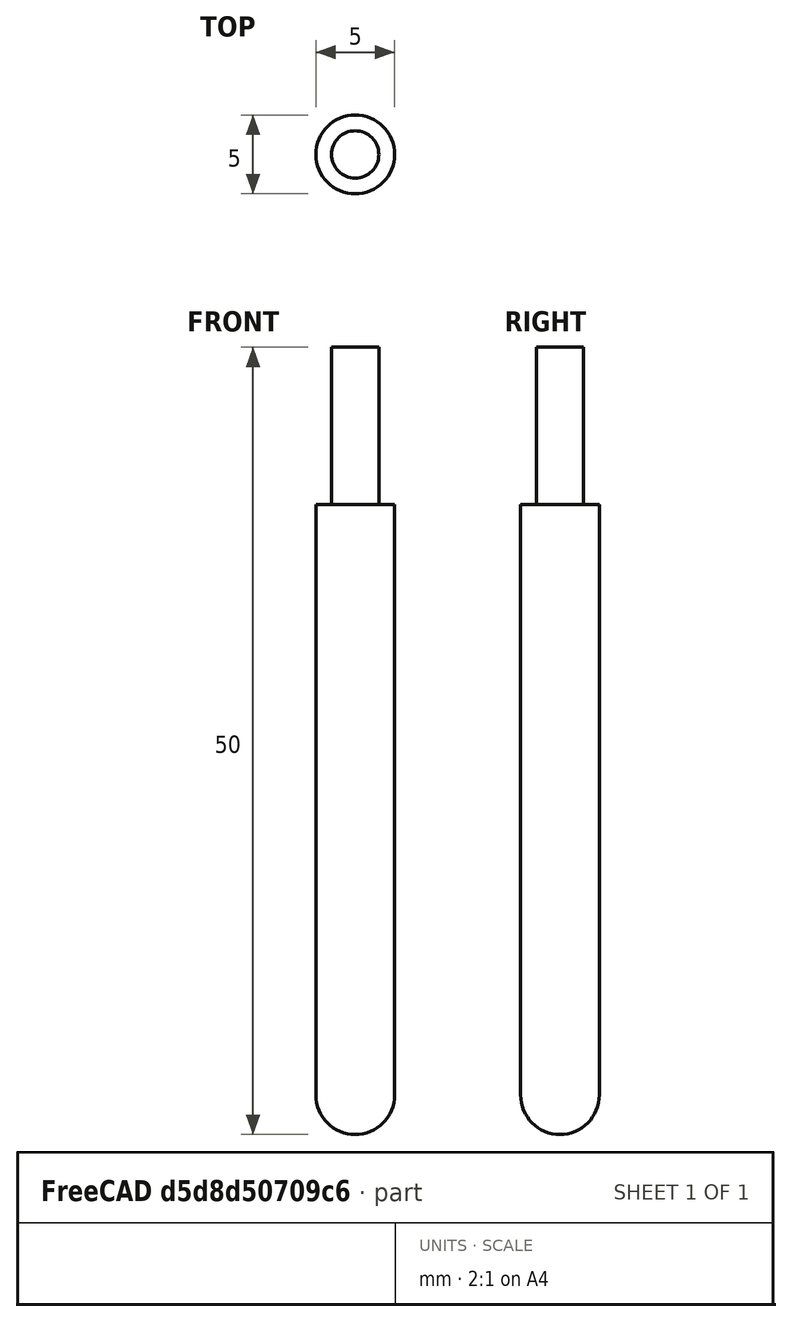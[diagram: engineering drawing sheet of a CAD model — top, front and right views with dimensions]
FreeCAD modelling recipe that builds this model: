
FCSTD DOCUMENT  (FreeCAD 0.19R24049 (Git))
Label: ballend
License: All rights reserved
LicenseURL: http://en.wikipedia.org/wiki/All_rights_reserved
objects: Sketcher::SketchObject×1, PartDesign::Revolution×1, App::FeaturePython×1, PartDesign::Body×1
note: 4 computed .brp shape members not serialized (recipe doc carries the construction recipe); baked Part::Feature solids carry a one-line shape summary decoded from their .brp

FEATURE [Sketcher::SketchObject] Sketch
  FullyConstrained = true
  MapMode = 5
  Placement = pos=(0,0,0) rot=(1,0,0;1.5708rad)
  Support = -> [XZ_Plane]
  expr: Constraints[10] = <<Attributes>>.ShankDiameter
  expr: Constraints[4] = <<Attributes>>.Length
  expr: Constraints[3] = <<Attributes>>.Diameter
  expr: Constraints[17] = <<Attributes>>.CuttingEdgeHeight
  sketch-geometry (8):
    g0: LineSegment StartX=-9e-16 StartY=50 StartZ=0 EndX=-9e-16 EndY=0 EndZ=0
    g1: LineSegment StartX=2.5 StartY=2.5 StartZ=0 EndX=2.5 EndY=40 EndZ=0
    g2: LineSegment StartX=1.5 StartY=50 StartZ=0 EndX=-9e-16 EndY=50 EndZ=0
    g3: LineSegment StartX=2.5 StartY=0 StartZ=0 EndX=-2.5 EndY=0 EndZ=0
    g4: LineSegment StartX=1.5 StartY=40.01 StartZ=0 EndX=2.5 EndY=40 EndZ=0
    g5: LineSegment StartX=1.5 StartY=50 StartZ=0 EndX=1.5 EndY=40.01 EndZ=0
    g6: LineSegment StartX=-1.5 StartY=50 StartZ=0 EndX=1.5 EndY=50 EndZ=0
    g7: ArcOfCircle CenterX=-5e-16 CenterY=2.5 CenterZ=0 NormalX=0 NormalY=0 NormalZ=1 AngleXU=0 Radius=2.5 StartAngle=4.71239 EndAngle=6.28319
  constraints (21):
    c: Vertical(g0)
    c: Vertical(g1)
    c: Horizontal(g2)
    c: DistanceX(g3,g3) = 5
    c: DistanceY(g3,g2) = 50
    c: Coincident(g1,g4)
    c: Vertical(g5)
    c: Coincident(g2,g5)
    c: Symmetric(g6,g6,g0)
    c: Coincident(g6,g2)
    c: DistanceX(g6,g6) = 3
    c: Coincident(g4,g5)
    c: Tangent(g1,g7) = -1.5708
    c: PointOnObject(g0,g3)
    c: Symmetric(g3,g3,g-2)
    c: Vertical(g3,g1)
    c: Perpendicular(g7,g0) = 4.71239
    c: DistanceY(g0,g1) = 40
    c: Coincident(g2,g0)
    c: Coincident(g0,g-1)
    c: DistanceY(g1,g4) = 0.01
FEATURE [PartDesign::Revolution] Revolution
  AllowMultiFace = false
  Angle = 360
  Axis = (0,-2e-16,1)
  Base = (0,0,0)
  Placement = pos=(0,0,0) rot=(1,0,0;1.5708rad)
  Profile = -> Sketch
  ReferenceAxis = -> Sketch [V_Axis]
  Reversed = true
FEATURE [App::FeaturePython] PropertyBag  label="Attributes"  # WARN: FeaturePython — macro-defined, semantics opaque (R4)
  Chipload = 0
  CustomPropertyGroups = Attributes | Shape
  CuttingEdgeHeight = 40
  Diameter = 5
  Flutes = 0
  Length = 50
  Material = 0
  ShankDiameter = 3
FEATURE [PartDesign::Body] Body  label="Ballend"
  Group = -> [Sketch,Revolution,PropertyBag]
  Origin = -> Origin
  Tip = -> Revolution
